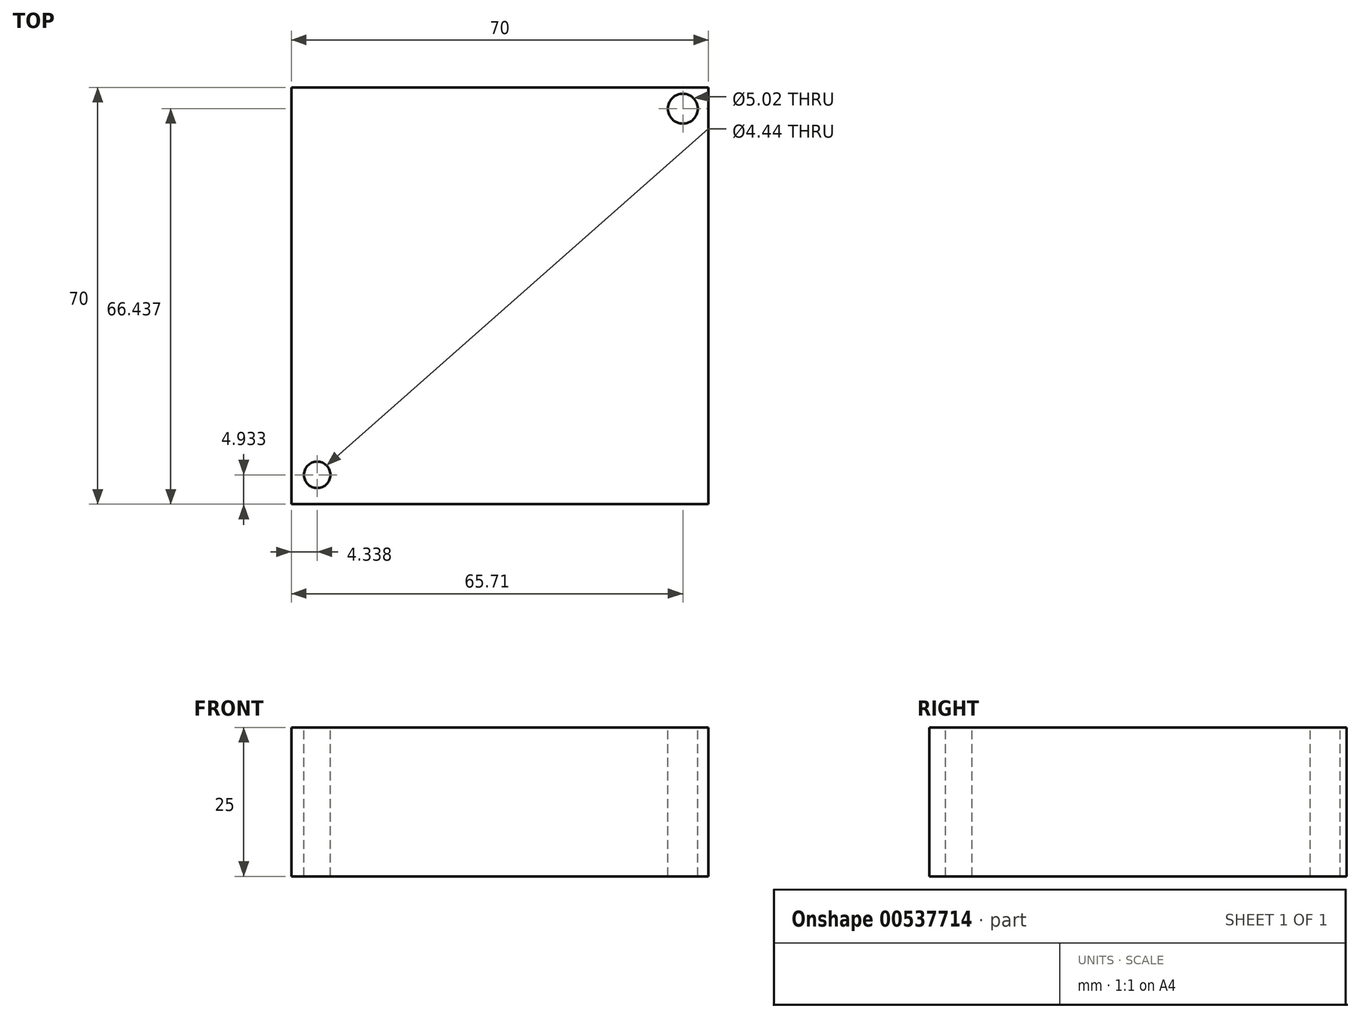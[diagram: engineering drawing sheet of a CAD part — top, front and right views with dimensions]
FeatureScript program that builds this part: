
annotation { "Feature Type Name" : "Feature", "Feature Type Description" : "" }
export const myFeature = defineFeature(function(context is Context, id is Id, definition is map)
    precondition{}
    {
        {
            var Q0;
            Q0=qCreatedBy(makeId("Top.planeOp"),FACE);
            var sketch = newSketch(context, id + "F0", { "sketchPlane" : qUnion([Q0])});
            skLineSegment(sketch, "E0.bottom", {"start": v(35, 35) * mm, "end": v(-35, 35) * mm});
            skLineSegment(sketch, "E0.top", {"start": v(35, -35) * mm, "end": v(-35, -35) * mm});
            skLineSegment(sketch, "E0.left", {"start": v(35, 35) * mm, "end": v(35, -35) * mm});
            skLineSegment(sketch, "E0.right", {"start": v(-35, 35) * mm, "end": v(-35, -35) * mm});
            skPoint(sketch, "E0.middle", {"position": v(0, 0) * mm});
            skLineSegment(sketch, "E1", {"start": v(-35, 35) * mm, "end": v(35, -35) * mm});
            skSolve(sketch);
        }
        {
            var Q0;
            Q0 = qSketchRegion(id + "F0", true);
            extrude(context, id + "F1", {"entities" : qUnion([Q0]), "endBound" : BoundingType.SYMMETRIC, "depth" : 25 * mm, "offsetDistance" : 25 * mm});
        }
        {
            var Q0;
            Q0=makeQuery(id+"F1.opExtrude","CAP_FACE",FACE,{"disambiguationData":[OSD([sQuery(id+"F0.wireOp",EDGE,"E0.bottom"),sQuery(id+"F0.wireOp",EDGE,"E0.top"),sQuery(id+"F0.wireOp",EDGE,"E0.left"),sQuery(id+"F0.wireOp",EDGE,"E0.right")])],"isStart":false});
            var sketch = newSketch(context, id + "F2", { "sketchPlane" : qUnion([Q0])});
            skCircle(sketch, "E2", {"center": v(-30.66, -30.07) * mm, "radius": 2.22 * mm});
            skCircle(sketch, "E3", {"center": v(30.71, 31.44) * mm, "radius": 2.5 * mm});
            skSolve(sketch);
        }
        {
            var Q0;
            Q0 = qSketchRegion(id + "F2", true);
            extrude(context, id + "F3", {"entities" : qUnion([Q0]), "operationType" : NewBodyOperationType.REMOVE, "oppositeDirection" : true, "depth" : 26 * mm, "offsetDistance" : 25 * mm});
        }
    });
